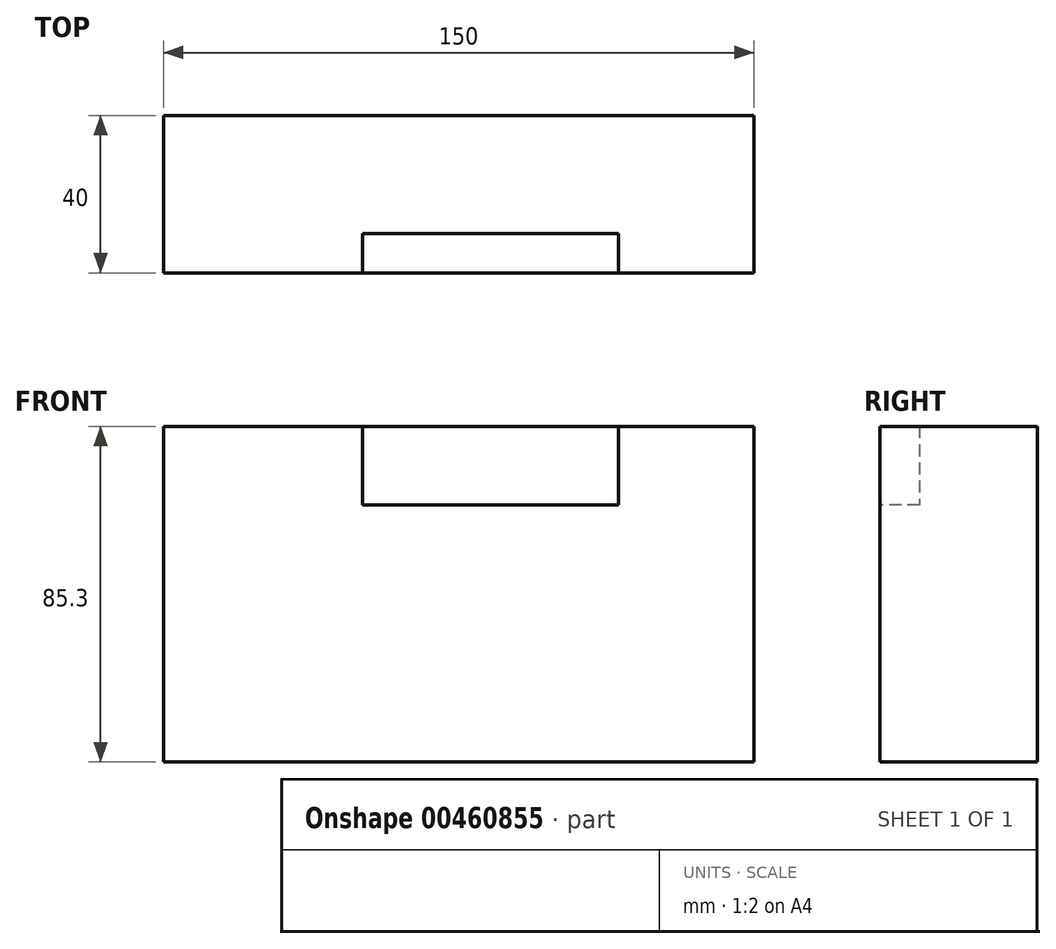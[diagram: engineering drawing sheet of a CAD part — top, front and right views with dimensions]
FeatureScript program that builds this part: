
annotation { "Feature Type Name" : "Feature", "Feature Type Description" : "" }
export const myFeature = defineFeature(function(context is Context, id is Id, definition is map)
    precondition{}
    {
        {
            var Q0;
            Q0=qCreatedBy(makeId("Top.planeOp"),FACE);
            var sketch = newSketch(context, id + "F0", { "sketchPlane" : qUnion([Q0])});
            skLineSegment(sketch, "E0.bottom", {"start": v(75, -27.15) * mm, "end": v(-75, -27.15) * mm});
            skLineSegment(sketch, "E0.top", {"start": v(75, 12.85) * mm, "end": v(-75, 12.85) * mm});
            skLineSegment(sketch, "E0.left", {"start": v(75, -27.15) * mm, "end": v(75, 12.85) * mm});
            skLineSegment(sketch, "E0.right", {"start": v(-75, -27.15) * mm, "end": v(-75, 12.85) * mm});
            skPoint(sketch, "E0.middle", {"position": v(0, -7.15) * mm});
            skSolve(sketch);
        }
        {
            var Q0;
            Q0 = qSketchRegion(id + "F0", true);
            extrude(context, id + "F1", {"entities" : qUnion([Q0]), "depth" : 85.3 * mm});
        }
        {
            var Q0;
            Q0=makeQuery(id+"F1.opExtrude","SWEPT_FACE",FACE,{"disambiguationData":[OSD([sQuery(id+"F0.wireOp",EDGE,"E0.bottom")])]});
            var sketch = newSketch(context, id + "F2", { "sketchPlane" : qUnion([Q0])});
            skLineSegment(sketch, "E1.bottom", {"start": v(-24.47, 85.3) * mm, "end": v(40.53, 85.3) * mm});
            skLineSegment(sketch, "E1.top", {"start": v(-24.47, 65.3) * mm, "end": v(40.53, 65.3) * mm});
            skLineSegment(sketch, "E1.left", {"start": v(-24.47, 85.3) * mm, "end": v(-24.47, 65.3) * mm});
            skLineSegment(sketch, "E1.right", {"start": v(40.53, 85.3) * mm, "end": v(40.53, 65.3) * mm});
            skSolve(sketch);
        }
        {
            var Q0;
            Q0=makeQuery(id+"F2.imprint","IMPRINT",FACE,{"disambiguationData":[TD([[makeQuery(id+"F2.imprint","IMPRINT",EDGE,{"derivedFrom":sQuery(id+"F2.wireOp",EDGE,"E1.bottom")}),1.0]])]});
            extrude(context, id + "F3", {"entities" : qUnion([Q0]), "operationType" : NewBodyOperationType.REMOVE, "oppositeDirection" : true, "depth" : 10 * mm});
        }
    });
